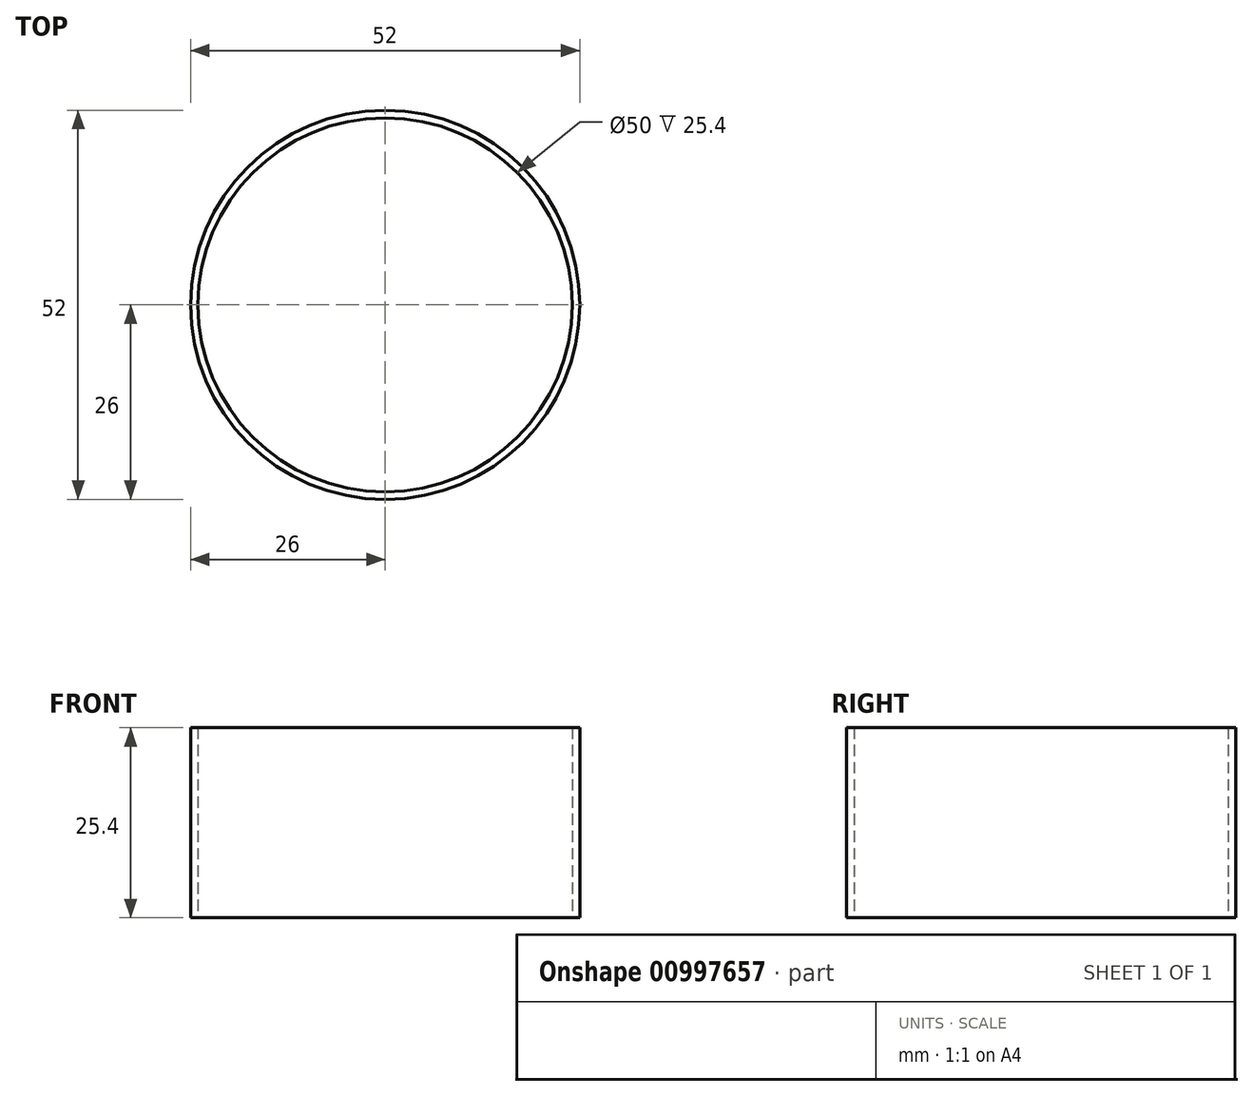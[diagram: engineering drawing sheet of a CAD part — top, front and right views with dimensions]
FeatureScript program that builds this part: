
annotation { "Feature Type Name" : "Feature", "Feature Type Description" : "" }
export const myFeature = defineFeature(function(context is Context, id is Id, definition is map)
    precondition{}
    {
        {
            var Q0;
            Q0=qCreatedBy(makeId("Top.planeOp"),FACE);
            var sketch = newSketch(context, id + "F0", { "sketchPlane" : qUnion([Q0])});
            skCircle(sketch, "E0", {"center": v(0, 0) * mm, "radius": 26 * mm});
            skCircle(sketch, "E1", {"center": v(0, 0) * mm, "radius": 25 * mm});
            skSolve(sketch);
        }
        {
            var Q0;
            Q0=qSketchRegion(id+"F0",true);
            extrude(context, id + "F1", {"entities" : qUnion([Q0]), "depth" : 25.4 * mm, "offsetDistance" : 25.4 * mm});
        }
    });
